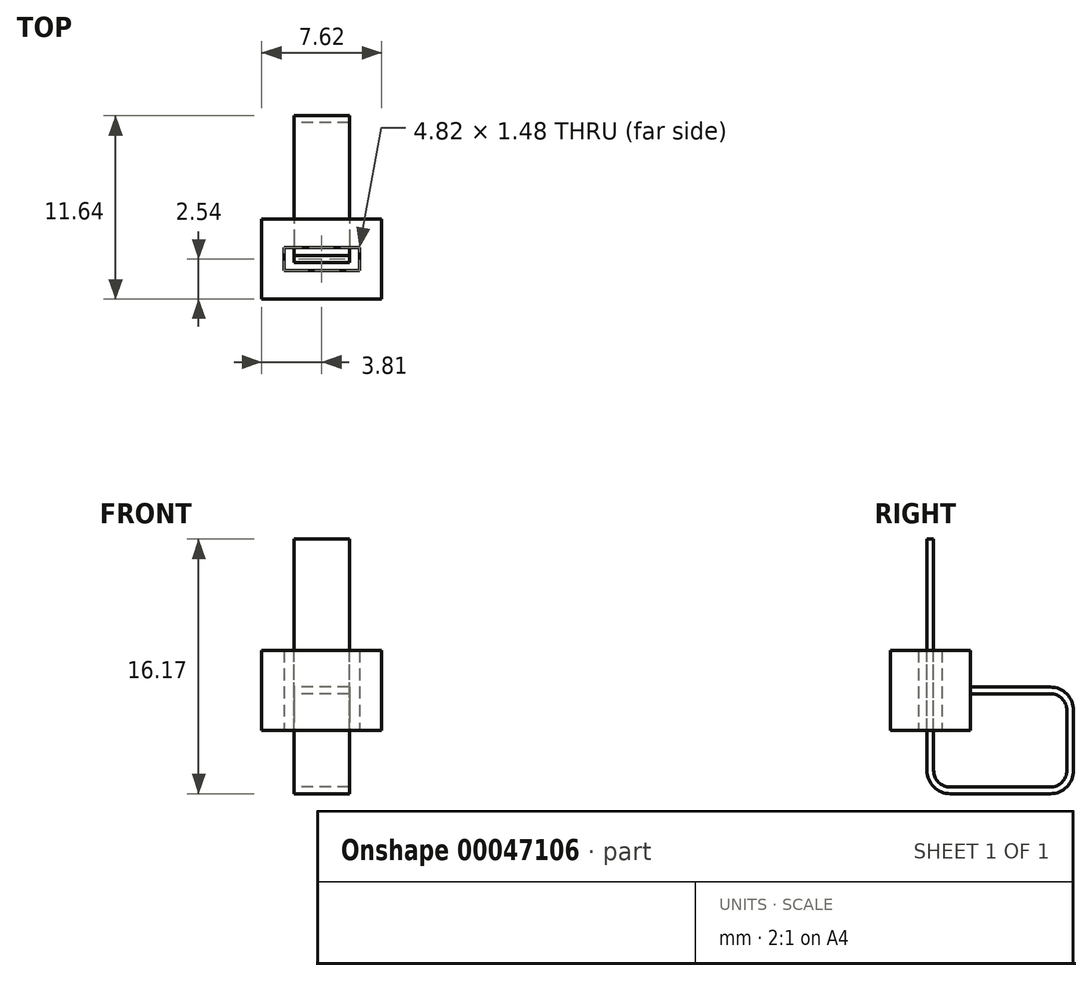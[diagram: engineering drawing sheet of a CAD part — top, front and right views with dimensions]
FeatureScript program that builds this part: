
annotation { "Feature Type Name" : "Feature", "Feature Type Description" : "" }
export const myFeature = defineFeature(function(context is Context, id is Id, definition is map)
    precondition{}
    {
        {
            var Q0;
            Q0=qCreatedBy(makeId("Right.planeOp"),FACE);
            var sketch = newSketch(context, id + "F0", { "sketchPlane" : qUnion([Q0])});
            skLineSegment(sketch, "E0.rect.bottom", {"start": v(2.54, 2.54) * mm, "end": v(-2.54, 2.54) * mm});
            skLineSegment(sketch, "E0.rect.top", {"start": v(2.54, -2.54) * mm, "end": v(-2.54, -2.54) * mm});
            skLineSegment(sketch, "E0.rect.left", {"start": v(2.54, 2.54) * mm, "end": v(2.54, -2.54) * mm});
            skLineSegment(sketch, "E0.rect.right", {"start": v(-2.54, 2.54) * mm, "end": v(-2.54, -2.54) * mm});
            skPoint(sketch, "E0.rect.middle", {"position": v(0, 0) * mm});
            skSolve(sketch);
        }
        {
            var Q0;
            Q0 = qSketchRegion(id + "F0", true);
            extrude(context, id + "F1", {"entities" : qUnion([Q0]), "endBound" : BoundingType.SYMMETRIC, "depth" : 7.62 * mm});
        }
        {
            var Q0;
            Q0=qCreatedBy(makeId("Right.planeOp"),FACE);
            var sketch = newSketch(context, id + "F2", { "sketchPlane" : qUnion([Q0])});
            skLineSegment(sketch, "E1", {"start": v(2.54, 0) * mm, "end": v(7.62, 0) * mm});
            skLineSegment(sketch, "E2", {"start": v(8.9, -1.27) * mm, "end": v(8.9, -5.08) * mm});
            skLineSegment(sketch, "E3", {"start": v(7.62, -6.35) * mm, "end": v(1.27, -6.35) * mm});
            skLineSegment(sketch, "E4", {"start": v(0, -5.08) * mm, "end": v(0, 9.6) * mm});
            skPoint(sketch, "E5.visualSharp", {"position": v(8.9, 0) * mm});
            skArc(sketch, "E5.filletArc", {"start": v(8.9, -1.27) * mm, "mid": v(8.52, -0.37) * mm, "end": v(7.62, 0) * mm});
            skPoint(sketch, "E6.visualSharp", {"position": v(8.9, -6.35) * mm});
            skArc(sketch, "E6.filletArc", {"start": v(7.62, -6.35) * mm, "mid": v(8.52, -5.98) * mm, "end": v(8.9, -5.08) * mm});
            skPoint(sketch, "E7.visualSharp", {"position": v(0, -6.35) * mm});
            skArc(sketch, "E7.filletArc", {"start": v(0, -5.08) * mm, "mid": v(0.37, -5.98) * mm, "end": v(1.27, -6.35) * mm});
            skPoint(sketch, "E8.orphan", {"position": v(0, 0) * mm});
            skPoint(sketch, "E9.orphan", {"position": v(2.54, 2.54) * mm});
            skPoint(sketch, "E10.0.end.orphan", {"position": v(2.54, -2.54) * mm});
            skSolve(sketch);
        }
        {
            var Q0;
            Q0=makeQuery(id+"F1.opExtrude","SWEPT_FACE",FACE,{"disambiguationData":[OSD([sQuery(id+"F0.wireOp",EDGE,"E0.rect.left")])]});
            var sketch = newSketch(context, id + "F3", { "sketchPlane" : qUnion([Q0])});
            skLineSegment(sketch, "E11.rect.bottom", {"start": v(-1.75, 0.21) * mm, "end": v(1.75, 0.21) * mm});
            skLineSegment(sketch, "E11.rect.top", {"start": v(-1.75, -0.21) * mm, "end": v(1.75, -0.21) * mm});
            skLineSegment(sketch, "E11.rect.left", {"start": v(-1.75, 0.21) * mm, "end": v(-1.75, -0.21) * mm});
            skLineSegment(sketch, "E11.rect.right", {"start": v(1.75, 0.21) * mm, "end": v(1.75, -0.21) * mm});
            skPoint(sketch, "E11.rect.middle", {"position": v(0, 0) * mm});
            skSolve(sketch);
        }
        {
            var Q0;
            Q0=makeQuery(id+"F3.imprint","IMPRINT",FACE,{"disambiguationData":[TD([[makeQuery(id+"F3.imprint","IMPRINT",EDGE,{"derivedFrom":sQuery(id+"F3.wireOp",EDGE,"E11.rect.bottom")}),-1.0]])]});
            var Q1;
            Q1=sQuery(id+"F2.wireOp",EDGE,"E1");
            var Q2;
            Q2=sQuery(id+"F2.wireOp",EDGE,"E5.filletArc");
            var Q3;
            Q3=sQuery(id+"F2.wireOp",EDGE,"E2");
            var Q4;
            Q4=sQuery(id+"F2.wireOp",EDGE,"E6.filletArc");
            var Q5;
            Q5=sQuery(id+"F2.wireOp",EDGE,"E3");
            var Q6;
            Q6=sQuery(id+"F2.wireOp",EDGE,"E7.filletArc");
            var Q7;
            Q7=sQuery(id+"F2.wireOp",EDGE,"E4");
            sweep(context, id + "F4", {"operationType" : NewBodyOperationType.ADD, "profiles" : qUnion([Q0]), "path" : qUnion([Q1, Q2, Q3, Q4, Q5, Q6, Q7])});
        }
        {
            var Q0;
            Q0=makeQuery(id+"F1.opExtrude","SWEPT_FACE",FACE,{"disambiguationData":[OSD([sQuery(id+"F0.wireOp",EDGE,"E0.rect.top")])]});
            var sketch = newSketch(context, id + "F5", { "sketchPlane" : qUnion([Q0])});
            skLineSegment(sketch, "E12.rect.bottom", {"start": v(2.4, 0.74) * mm, "end": v(-2.4, 0.74) * mm});
            skLineSegment(sketch, "E12.rect.top", {"start": v(2.4, -0.74) * mm, "end": v(-2.4, -0.74) * mm});
            skLineSegment(sketch, "E12.rect.left", {"start": v(2.4, 0.74) * mm, "end": v(2.4, -0.74) * mm});
            skLineSegment(sketch, "E12.rect.right", {"start": v(-2.4, 0.74) * mm, "end": v(-2.4, -0.74) * mm});
            skPoint(sketch, "E12.rect.middle", {"position": v(0, 0) * mm});
            skSolve(sketch);
        }
        {
            var Q0;
            Q0=makeQuery(id+"F5.imprint","IMPRINT",FACE,{"disambiguationData":[TD([[makeQuery(id+"F5.imprint","IMPRINT",EDGE,{"derivedFrom":sQuery(id+"F5.wireOp",EDGE,"E12.rect.bottom")}),1.0]])]});
            extrude(context, id + "F6", {"entities" : qUnion([Q0]), "operationType" : NewBodyOperationType.REMOVE, "endBound" : BoundingType.UP_TO_NEXT, "oppositeDirection" : true, "depth" : 25.4 * mm});
        }
    });
